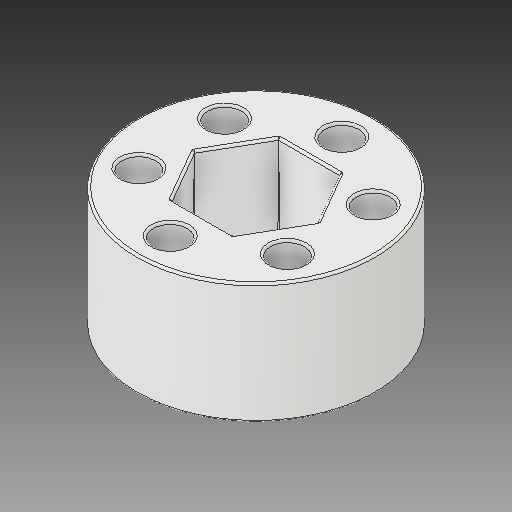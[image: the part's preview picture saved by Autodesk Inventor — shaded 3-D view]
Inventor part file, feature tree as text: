
AUTODESK INVENTOR PART (.ipt)
format: ipt  version: 2018.2 (Build 222227000, 227)  size: 248,832 bytes
history: native  units: in
note: dims shown in document units (in); Inventor stores cm internally (conversion verified against a paired STEP export)
features: fillet x1
ambient origin geometry x8: Origin, YZ Plane, XZ Plane, XY Plane, X Axis, Y Axis, Z Axis, Center Point
bodies: Solid1 (feature_tree)
feature tree (1):
  fillet  "Fillet2"  [1 undecoded]
note: 1 required parameter value undecoded (feature->parameter linkage not recoverable at this tier; creation-order binding heuristic only, values carry confidence <= 0.55)
